# Revit family: Wire-Array-HunterDouglas-Hook-On
name_source: partatom
category: Specialty Equipment
revit_build: Autodesk Revit Architecture 2013 (Build: 20120221_2030(x64)
units: mm (PartAtom-declared; Revit-internal decimal feet)

## types (1)
- Parametric
    04 CSI = 09 51 00
    95 CSI = 09510
    Assembly Code = C3030200
    Color Finishes = http://www.hunterdouglascontract.com
    Default Elevation = 0' - 0"
    Description = Wire Array
    Manufacturer = Hunter Douglas Luxalon Metal Ceilings
    Model = Hook-On Wire Array
    Perforations = http://www.hunterdouglascontract.com
    Product Line = Hook-On
    Spacing = 4' - 0"
    Subcategory = Metal - Plank and Tile
    URL = http://www.hunterdouglascontract.com
    Wire = Metal - Aluminum Frame - HunterDouglas - Painted White
    ecoScorecard Product Page = http://hunterdouglascontract.ecoscorecard.com
    ecoScorecard_data = http://products.ecoscorecard.com

## geometry (parser evidence)
native form markers: Sweep x3
no freeform markers — native parametric forms only
